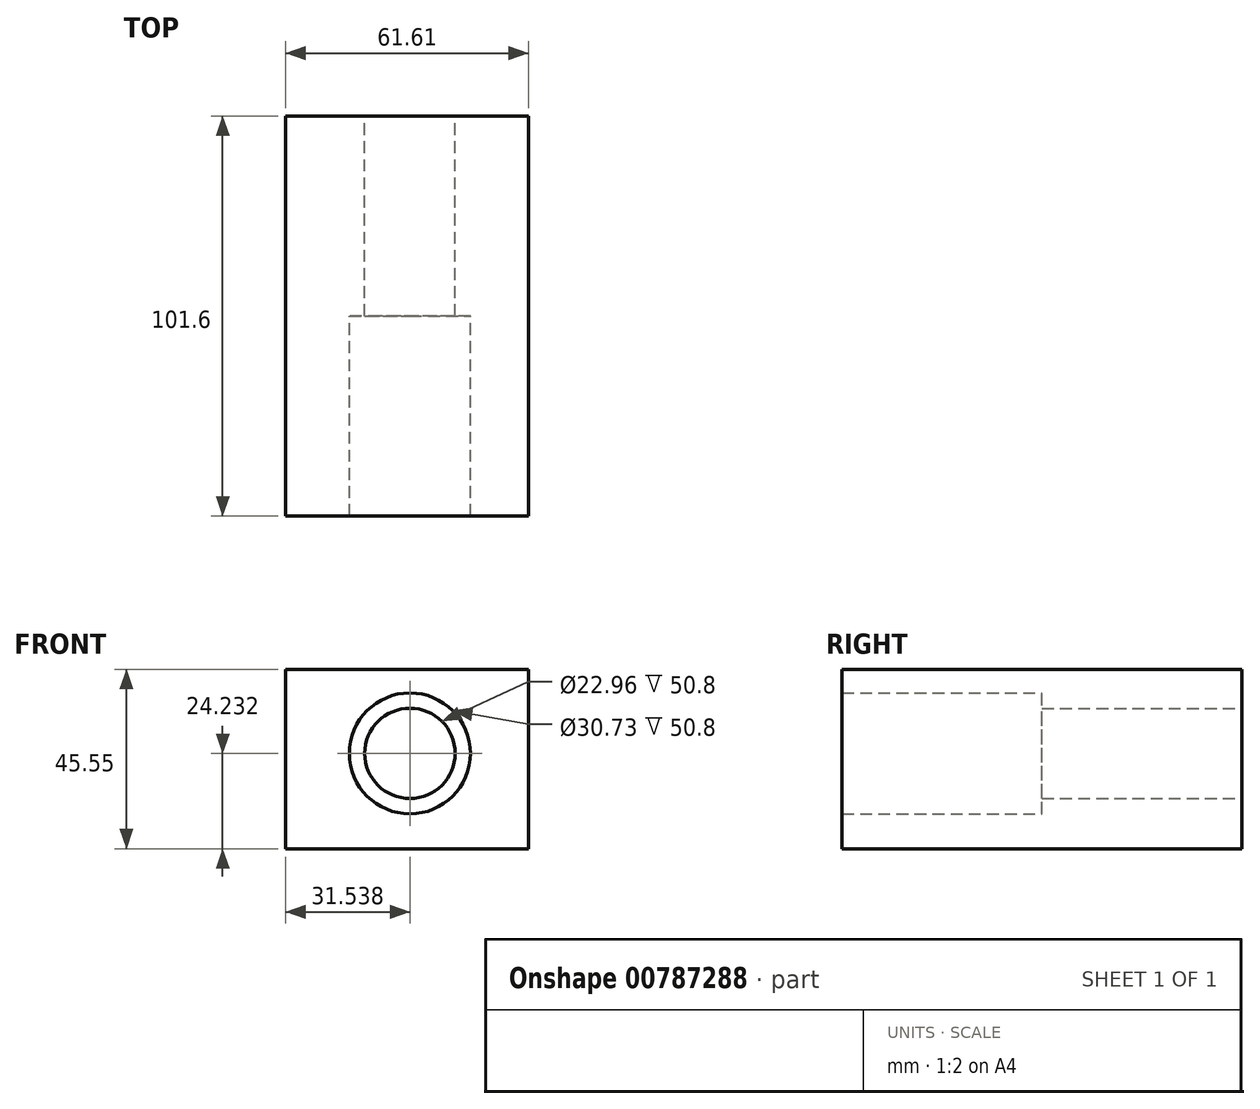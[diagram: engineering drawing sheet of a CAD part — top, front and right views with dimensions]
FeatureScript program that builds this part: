
annotation { "Feature Type Name" : "Feature", "Feature Type Description" : "" }
export const myFeature = defineFeature(function(context is Context, id is Id, definition is map)
    precondition{}
    {
        {
            var Q0;
            Q0=qCreatedBy(makeId("Front.planeOp"),FACE);
            var sketch = newSketch(context, id + "F0", { "sketchPlane" : qUnion([Q0])});
            skLineSegment(sketch, "E0", {"start": v(-26.72, 31.1) * mm, "end": v(34.9, 31.1) * mm});
            skLineSegment(sketch, "E1", {"start": v(34.9, -14.45) * mm, "end": v(34.9, 31.1) * mm});
            skLineSegment(sketch, "E2", {"start": v(-26.72, 31.1) * mm, "end": v(-26.72, -14.45) * mm});
            skLineSegment(sketch, "E3", {"start": v(34.9, -14.45) * mm, "end": v(-26.72, -14.45) * mm});
            skCircle(sketch, "E4", {"center": v(4.82, 9.78) * mm, "radius": 15.36 * mm});
            skCircle(sketch, "E5", {"center": v(4.82, 9.78) * mm, "radius": 11.48 * mm});
            skSolve(sketch);
        }
        {
            var Q0;
            Q0=makeQuery(id+"F0.imprint","IMPRINT",FACE,{"disambiguationData":[TD([[makeQuery(id+"F0.imprint","IMPRINT",EDGE,{"derivedFrom":sQuery(id+"F0.wireOp",EDGE,"E4")}),1.0]])]});
            var Q1;
            Q1=makeQuery(id+"F0.imprint","IMPRINT",FACE,{"disambiguationData":[TD([[makeQuery(id+"F0.imprint","IMPRINT",EDGE,{"derivedFrom":sQuery(id+"F0.wireOp",EDGE,"E0")}),-1.0]])]});
            extrude(context, id + "F1", {"entities" : qUnion([Q0, Q1]), "depth" : 50.8 * mm, "offsetDistance" : 25.4 * mm});
        }
        {
            var Q0;
            Q0 = qSketchRegion(id + "F0", true);
            extrude(context, id + "F2", {"entities" : qUnion([Q0]), "operationType" : NewBodyOperationType.ADD, "depth" : 101.6 * mm, "offsetDistance" : 25.4 * mm});
        }
        {
            var Q0;
            Q0=sQuery(id+"F0.wireOp",EDGE,"E5");
            var Q1;
            Q1=sQuery(id+"F0.wireOp",EDGE,"E4");
            extrude(context, id + "F3", {"bodyType" : ToolBodyType.SURFACE, "surfaceEntities" : qUnion([Q0, Q1]), "depth" : 127 * mm, "offsetDistance" : 25.4 * mm});
        }
    });
